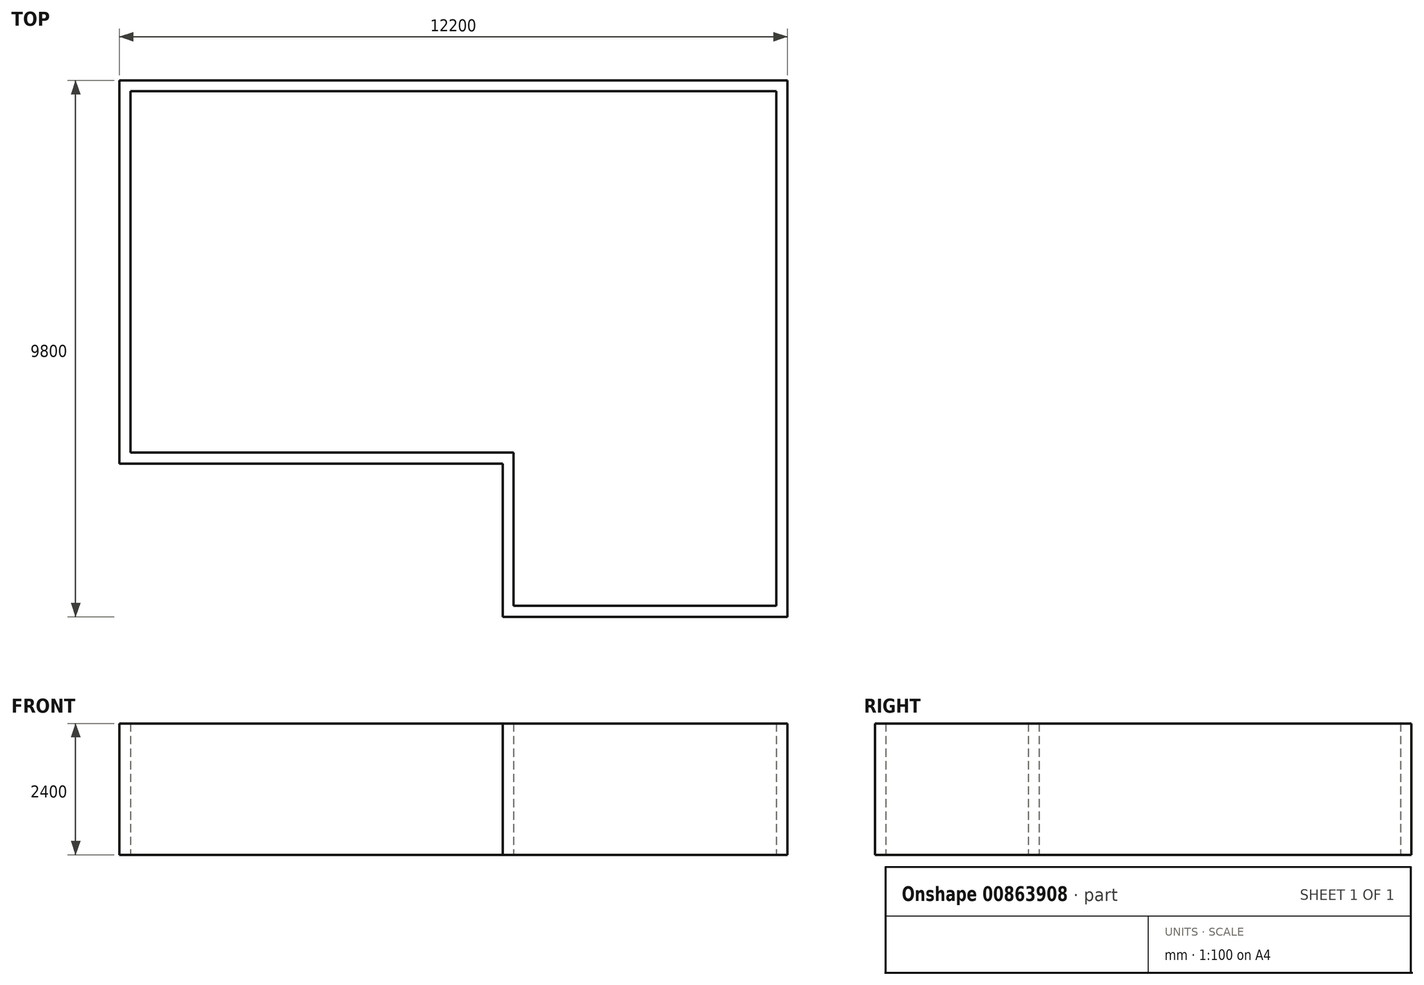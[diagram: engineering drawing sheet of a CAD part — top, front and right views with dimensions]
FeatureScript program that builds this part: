
annotation { "Feature Type Name" : "Feature", "Feature Type Description" : "" }
export const myFeature = defineFeature(function(context is Context, id is Id, definition is map)
    precondition{}
    {
        {
            var Q0;
            Q0=qCreatedBy(makeId("Top.planeOp"),FACE);
            var sketch = newSketch(context, id + "F0", { "sketchPlane" : qUnion([Q0])});
            skLineSegment(sketch, "E0", {"start": v(-128344.97, 60627.92) * mm, "end": v(-116144.97, 60627.92) * mm});
            skLineSegment(sketch, "E1", {"start": v(-116144.97, 60627.92) * mm, "end": v(-116144.97, 50827.92) * mm});
            skLineSegment(sketch, "E2", {"start": v(-116144.97, 50827.92) * mm, "end": v(-121344.97, 50827.92) * mm});
            skLineSegment(sketch, "E3", {"start": v(-121344.97, 50827.92) * mm, "end": v(-121344.97, 53627.92) * mm});
            skLineSegment(sketch, "E4", {"start": v(-121344.97, 53627.92) * mm, "end": v(-128344.97, 53627.92) * mm});
            skLineSegment(sketch, "E5", {"start": v(-128344.97, 53627.92) * mm, "end": v(-128344.97, 60627.92) * mm});
            skLineSegment(sketch, "E6", {"start": v(-121344.97, 50827.92) * mm, "end": v(-121146.97, 50827.92) * mm});
            skLineSegment(sketch, "E7.0", {"start": v(-128146.97, 53825.92) * mm, "end": v(-128146.97, 60429.92) * mm});
            skLineSegment(sketch, "E7.1", {"start": v(-116342.97, 60429.92) * mm, "end": v(-116342.97, 51025.92) * mm});
            skLineSegment(sketch, "E7.2", {"start": v(-116342.97, 51025.92) * mm, "end": v(-121146.97, 51025.92) * mm});
            skLineSegment(sketch, "E7.3", {"start": v(-128146.97, 60429.92) * mm, "end": v(-116342.97, 60429.92) * mm});
            skLineSegment(sketch, "E7.4", {"start": v(-121146.97, 51025.92) * mm, "end": v(-121146.97, 53825.92) * mm});
            skLineSegment(sketch, "E7.5", {"start": v(-121146.97, 53825.92) * mm, "end": v(-128146.97, 53825.92) * mm});
            skSolve(sketch);
        }
        {
            var Q0;
            Q0=qSketchRegion(id+"F0",true);
            extrude(context, id + "F1", {"entities" : qUnion([Q0]), "surfaceOperationType" : NewSurfaceOperationType.ADD, "depth" : 2400 * mm, "offsetDistance" : 25 * mm});
        }
    });
